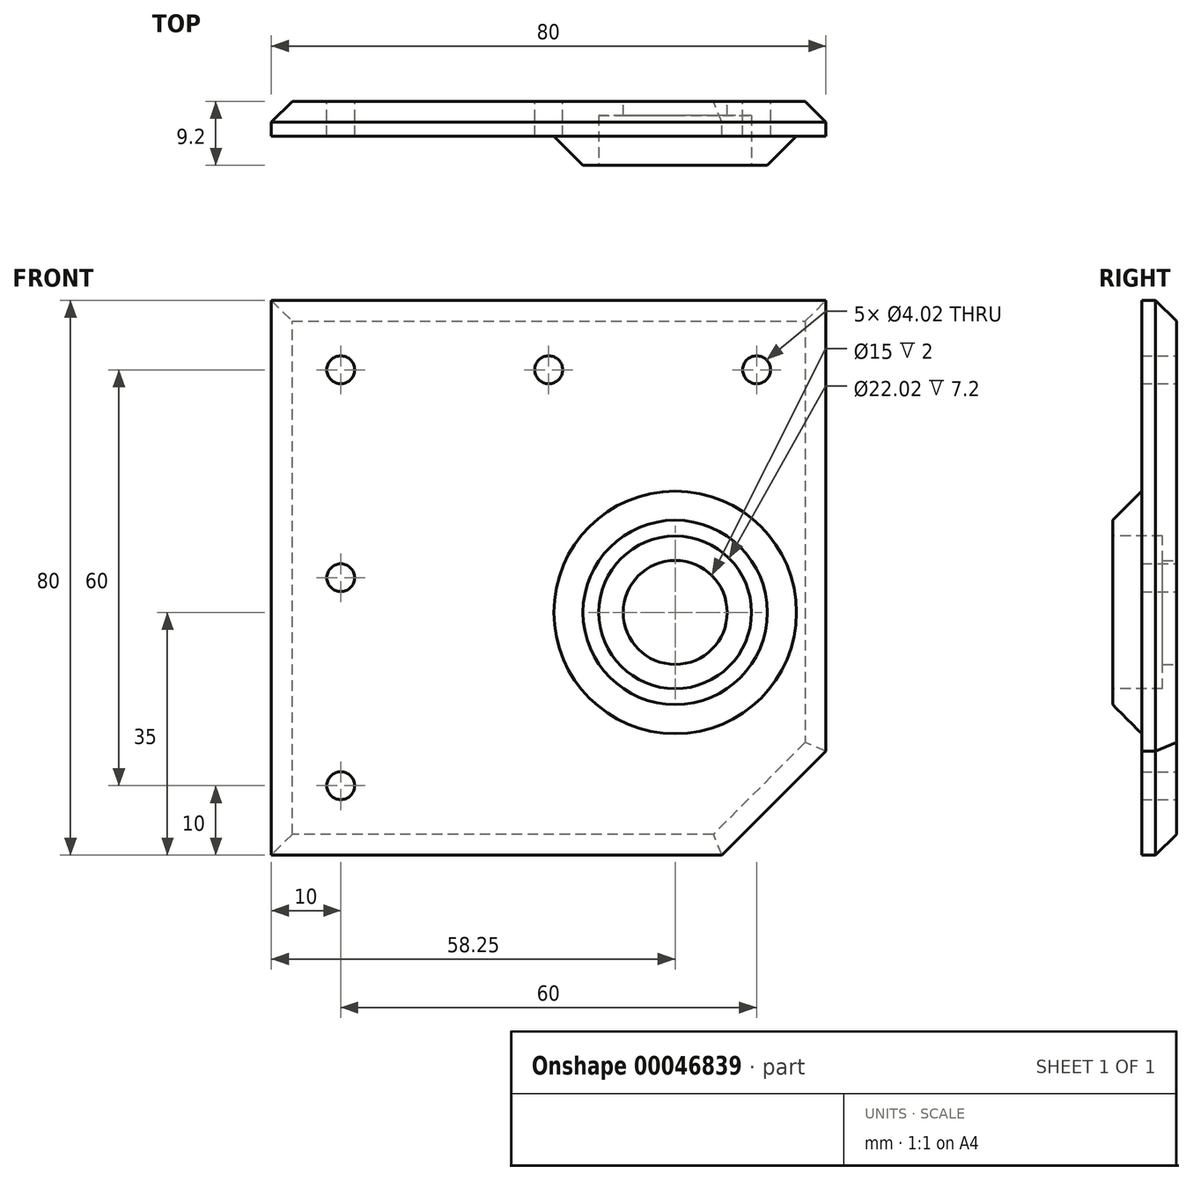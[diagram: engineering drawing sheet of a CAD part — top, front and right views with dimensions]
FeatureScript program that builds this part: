
annotation { "Feature Type Name" : "Feature", "Feature Type Description" : "" }
export const myFeature = defineFeature(function(context is Context, id is Id, definition is map)
    precondition{}
    {
        {
            var Q0;
            Q0=qCreatedBy(makeId("Front.planeOp"),FACE);
            var sketch = newSketch(context, id + "F0", { "sketchPlane" : qUnion([Q0])});
            skLineSegment(sketch, "E0", {"start": v(0, 0) * mm, "end": v(0, 80) * mm});
            skLineSegment(sketch, "E1", {"start": v(0, 80) * mm, "end": v(80, 80) * mm});
            skLineSegment(sketch, "E2", {"start": v(80, 80) * mm, "end": v(80, 60) * mm, "construction": true});
            skLineSegment(sketch, "E3", {"start": v(80, 60) * mm, "end": v(20, 60) * mm, "construction": true});
            skLineSegment(sketch, "E4", {"start": v(20, 60) * mm, "end": v(20, 0) * mm, "construction": true});
            skLineSegment(sketch, "E5", {"start": v(20, 0) * mm, "end": v(0, 0) * mm, "construction": true});
            skCircle(sketch, "E6", {"center": v(58.25, 35) * mm, "radius": 7.5 * mm});
            skLineSegment(sketch, "E7", {"start": v(80, 80) * mm, "end": v(80, 15) * mm});
            skLineSegment(sketch, "E8", {"start": v(65, 0) * mm, "end": v(0, 0) * mm});
            skCircle(sketch, "E9", {"center": v(10, 70) * mm, "radius": 2 * mm});
            skCircle(sketch, "E10", {"center": v(40, 70) * mm, "radius": 2 * mm});
            skCircle(sketch, "E11", {"center": v(70, 70) * mm, "radius": 2 * mm});
            skCircle(sketch, "E12", {"center": v(10, 40) * mm, "radius": 2 * mm});
            skCircle(sketch, "E13", {"center": v(10, 10) * mm, "radius": 2 * mm});
            skLineSegment(sketch, "E14", {"start": v(65, 0) * mm, "end": v(80, 15) * mm});
            skPoint(sketch, "E15.orphan", {"position": v(80, 0) * mm});
            skSolve(sketch);
        }
        {
            var Q0;
            Q0=qSketchRegion(id+"F0",true);
            extrude(context, id + "F1", {"entities" : qUnion([Q0]), "depth" : 5 * mm});
        }
        {
            var Q0;
            Q0=makeQuery(id+"F1.opExtrude","CAP_FACE",FACE,{"disambiguationData":[OSD([sQuery(id+"F0.wireOp",EDGE,"E0"),sQuery(id+"F0.wireOp",EDGE,"E1"),sQuery(id+"F0.wireOp",EDGE,"E6"),sQuery(id+"F0.wireOp",EDGE,"E7"),sQuery(id+"F0.wireOp",EDGE,"E8"),sQuery(id+"F0.wireOp",EDGE,"E9"),sQuery(id+"F0.wireOp",EDGE,"E10"),sQuery(id+"F0.wireOp",EDGE,"E11"),sQuery(id+"F0.wireOp",EDGE,"E12"),sQuery(id+"F0.wireOp",EDGE,"E13"),sQuery(id+"F0.wireOp",EDGE,"E14")])],"isStart":false});
            var sketch = newSketch(context, id + "F2", { "sketchPlane" : qUnion([Q0])});
            skCircle(sketch, "E16", {"center": v(58.25, 35) * mm, "radius": 11.01 * mm});
            skSolve(sketch);
        }
        {
            var Q0;
            Q0=qSketchRegion(id+"F2",true);
            extrude(context, id + "F3", {"entities" : qUnion([Q0]), "operationType" : NewBodyOperationType.REMOVE, "oppositeDirection" : true, "depth" : 3 * mm});
        }
        {
            var Q0;
            Q0=makeQuery(id+"F1.opExtrude","CAP_FACE",FACE,{"disambiguationData":[OSD([sQuery(id+"F0.wireOp",EDGE,"E0"),sQuery(id+"F0.wireOp",EDGE,"E1"),sQuery(id+"F0.wireOp",EDGE,"E6"),sQuery(id+"F0.wireOp",EDGE,"E7"),sQuery(id+"F0.wireOp",EDGE,"E8"),sQuery(id+"F0.wireOp",EDGE,"E9"),sQuery(id+"F0.wireOp",EDGE,"E10"),sQuery(id+"F0.wireOp",EDGE,"E11"),sQuery(id+"F0.wireOp",EDGE,"E12"),sQuery(id+"F0.wireOp",EDGE,"E13"),sQuery(id+"F0.wireOp",EDGE,"E14")])],"isStart":false});
            var sketch = newSketch(context, id + "F4", { "sketchPlane" : qUnion([Q0])});
            skCircle(sketch, "E17", {"center": v(58.25, 35) * mm, "radius": 17.5 * mm});
            skCircle(sketch, "E18", {"center": v(58.25, 35) * mm, "radius": 11.01 * mm});
            skSolve(sketch);
        }
        {
            var Q0;
            Q0=qSketchRegion(id+"F4",true);
            extrude(context, id + "F5", {"entities" : qUnion([Q0]), "operationType" : NewBodyOperationType.ADD, "depth" : 4.2 * mm});
        }
        {
            var Q0;
            Q0=makeQuery(id+"F5.opExtrude","CAP_EDGE",EDGE,{"disambiguationData":[OSD([sQuery(id+"F4.wireOp",EDGE,"E17")])],"isStart":false});
            chamfer(context, id + "F6", {"entities" : qUnion([Q0]), "width" : 4.2 * mm, "tangentPropagation" : true});
        }
        {
            var Q0;
            Q0=makeQuery(id+"F1.opExtrude","CAP_EDGE",EDGE,{"disambiguationData":[OSD([sQuery(id+"F0.wireOp",EDGE,"E1")])],"isStart":true});
            var Q1;
            Q1=makeQuery(id+"F1.opExtrude","CAP_EDGE",EDGE,{"disambiguationData":[OSD([sQuery(id+"F0.wireOp",EDGE,"E7")])],"isStart":true});
            var Q2;
            Q2=makeQuery(id+"F1.opExtrude","CAP_EDGE",EDGE,{"disambiguationData":[OSD([sQuery(id+"F0.wireOp",EDGE,"E14")])],"isStart":true});
            var Q3;
            Q3=makeQuery(id+"F1.opExtrude","CAP_EDGE",EDGE,{"disambiguationData":[OSD([sQuery(id+"F0.wireOp",EDGE,"E0")])],"isStart":true});
            var Q4;
            Q4=makeQuery(id+"F1.opExtrude","CAP_EDGE",EDGE,{"disambiguationData":[OSD([sQuery(id+"F0.wireOp",EDGE,"E8")])],"isStart":true});
            chamfer(context, id + "F7", {"entities" : qUnion([Q0, Q1, Q2, Q3, Q4]), "width" : 3 * mm, "tangentPropagation" : true});
        }
        {
            var Q0;
            Q0=makeQuery(id+"F1.opExtrude","SWEPT_BODY",BODY,{"disambiguationData":[OSD([sQuery(id+"F0.wireOp",EDGE,"E0"),sQuery(id+"F0.wireOp",EDGE,"E1"),sQuery(id+"F0.wireOp",EDGE,"E6"),sQuery(id+"F0.wireOp",EDGE,"E7"),sQuery(id+"F0.wireOp",EDGE,"E8"),sQuery(id+"F0.wireOp",EDGE,"E9"),sQuery(id+"F0.wireOp",EDGE,"E10"),sQuery(id+"F0.wireOp",EDGE,"E11"),sQuery(id+"F0.wireOp",EDGE,"E12"),sQuery(id+"F0.wireOp",EDGE,"E13"),sQuery(id+"F0.wireOp",EDGE,"E14")])]});
            transform(context, id + "F8", {"entities" : qUnion([Q0]), "transformType" : TransformType.TRANSLATION_3D, "dx" : 0 * mm, "dy" : 0 * mm, "dz" : 0 * mm, "makeCopy" : true});
        }
        {
            var Q0;
            Q0=makeQuery(id+"F8.opPattern","COPY",BODY,{"derivedFrom":makeQuery(id+"F1.opExtrude","SWEPT_BODY",BODY,{"disambiguationData":[OSD([sQuery(id+"F0.wireOp",EDGE,"E0"),sQuery(id+"F0.wireOp",EDGE,"E1"),sQuery(id+"F0.wireOp",EDGE,"E6"),sQuery(id+"F0.wireOp",EDGE,"E7"),sQuery(id+"F0.wireOp",EDGE,"E8"),sQuery(id+"F0.wireOp",EDGE,"E9"),sQuery(id+"F0.wireOp",EDGE,"E10"),sQuery(id+"F0.wireOp",EDGE,"E11"),sQuery(id+"F0.wireOp",EDGE,"E12"),sQuery(id+"F0.wireOp",EDGE,"E13"),sQuery(id+"F0.wireOp",EDGE,"E14")])]}),"instanceName":"1"});
            deleteBodies(context, id + "F9", {"entities" : qUnion([Q0])});
        }
    });
